# Revit family: Detail_Batten_Knotwood_SelfMating
name_source: partatom
category: Detail Items
units: mm (PartAtom-declared; Revit-internal decimal feet)

## family parameters
Rotate with component = No
Section Shape = Not Defined
Shared = No

## types (4) — shared parameters
Description = Knotwood Self Mating Batten (KESM10016)
Manufacturer = Knotwood
ManufacturerOverallDepth = 16 mm  [stored 0.0524934 ft]
ManufacturerURLProductSpecific = https://www.knotwood.com.au
ModifiedIssue = 20231110 $
URL = https://www.knotwood.com.au

## per-type parameters (varying)
| type | FemaleType | ManufacturerOverallWidth | ManufacturerSpecCode | Model |
| 65mm (KESM6516) | z_DetailItem_Batten_Knotwood_SelfMating_6516 : KESM6516 | 65 mm  [stored 0.213255 ft] | KESM6516 | KESM6516 |
| 38mm (KESM3816) | z_DetailItem_Batten_Knotwood_SelfMating_3816 : KESM3816 | 38 mm  [stored 0.124672 ft] | KESM3816 | KESM3816 |
| 100mm (KESM10016) | z_DetailItem_Batten_Knotwood_SelfMating_10016 : KESM10016 | 100 mm  [stored 0.328084 ft] | KESM10016 | KESM10016 |
| 150mm (KESM15016) | z_DetailItem_Batten_Knotwood_SelfMating_15016 : KESM15016 | 150 mm  [stored 0.492126 ft] | KESM15016 | KESM15016 |

note: [stored X ft] marks values corroborated as IEEE doubles in the binary element streams (Revit-internal decimal feet)

## geometry (parser evidence)
native form markers: Sweep x2
no freeform markers — native parametric forms only
